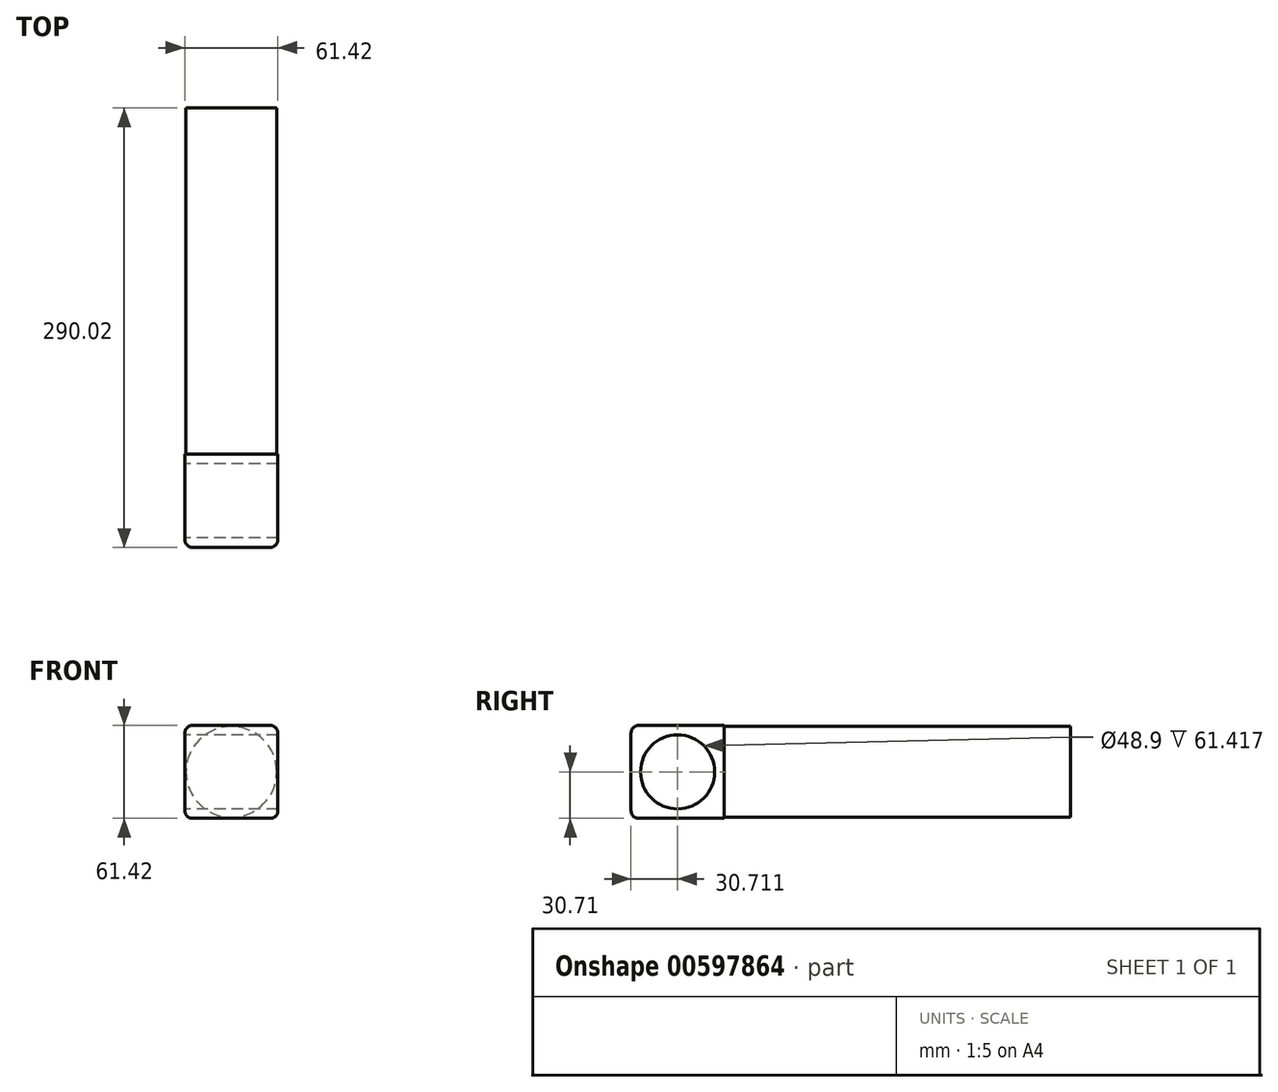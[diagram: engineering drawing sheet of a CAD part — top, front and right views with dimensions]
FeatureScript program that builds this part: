
annotation { "Feature Type Name" : "Feature", "Feature Type Description" : "" }
export const myFeature = defineFeature(function(context is Context, id is Id, definition is map)
    precondition{}
    {
        {
            var Q0;
            Q0=qCreatedBy(makeId("Front.planeOp"),FACE);
            var sketch = newSketch(context, id + "F0", { "sketchPlane" : qUnion([Q0])});
            skCircle(sketch, "E0", {"center": v(0, 0) * mm, "radius": 29.97 * mm});
            skSolve(sketch);
        }
        {
            var Q0;
            Q0=makeQuery(id+"F0.imprint","IMPRINT",FACE,{"disambiguationData":[TD([[makeQuery(id+"F0.imprint","IMPRINT",EDGE,{"derivedFrom":sQuery(id+"F0.wireOp",EDGE,"E0")}),1.0]])]});
            extrude(context, id + "F1", {"entities" : qUnion([Q0]), "oppositeDirection" : true, "depth" : 228.6 * mm, "offsetDistance" : 25.4 * mm});
        }
        {
            var Q0;
            Q0=qCreatedBy(makeId("Front.planeOp"),FACE);
            var sketch = newSketch(context, id + "F2", { "sketchPlane" : qUnion([Q0])});
            skLineSegment(sketch, "E1.bottom", {"start": v(-30.7, 30.71) * mm, "end": v(30.7, 30.71) * mm});
            skLineSegment(sketch, "E1.top", {"start": v(-30.7, -30.71) * mm, "end": v(30.7, -30.71) * mm});
            skLineSegment(sketch, "E1.left", {"start": v(-30.7, 30.71) * mm, "end": v(-30.7, -30.71) * mm});
            skLineSegment(sketch, "E1.right", {"start": v(30.7, 30.71) * mm, "end": v(30.7, -30.71) * mm});
            skPoint(sketch, "E1.middle", {"position": v(0, 0) * mm});
            skSolve(sketch);
        }
        {
            var Q0;
            Q0 = qSketchRegion(id + "F2", true);
            extrude(context, id + "F3", {"entities" : qUnion([Q0]), "operationType" : NewBodyOperationType.ADD, "depth" : 61.42 * mm, "offsetDistance" : 25.4 * mm});
        }
        {
            var Q0;
            Q0=makeQuery(id+"F3.opExtrude","SWEPT_FACE",FACE,{"disambiguationData":[OSD([sQuery(id+"F2.wireOp",EDGE,"E1.left")])]});
            var sketch = newSketch(context, id + "F4", { "sketchPlane" : qUnion([Q0])});
            skCircle(sketch, "E2", {"center": v(30.7, 0) * mm, "radius": 24.45 * mm});
            skPoint(sketch, "E2.centerSnap0", {"position": v(30.7, 30.71) * mm});
            skSolve(sketch);
        }
        {
            var Q0;
            Q0=sQuery(id+"F4.wireOp",VERTEX,"E2.center");
            var Q1;
            Q1=makeQuery(id+"F1.opExtrude","SWEPT_BODY",BODY,{"disambiguationData":[OSD([sQuery(id+"F0.wireOp",EDGE,"E0")])]});
            hole(context, id + "F5", {"style" : HoleStyle.SIMPLE, "endStyle" : HoleEndStyle.THROUGH, "holeDiameter" : 48.9 * mm, "majorDiameter" : 6.35 * mm, "isTappedThrough" : true, "tappedDepth" : 12.7 * mm, "tapClearance" : 3, "locations" : qUnion([Q0]), "scope" : qUnion([Q1])});
        }
        {
            var Q0;
            Q0=makeQuery(id+"F3.opExtrude","SWEPT_EDGE",EDGE,{"disambiguationData":[OSD([sQuery(id+"F2.wireOp",EDGE,"E1.bottom"),sQuery(id+"F2.wireOp",EDGE,"E1.left")])]});
            var Q1;
            Q1=makeQuery(id+"F3.opExtrude","CAP_EDGE",EDGE,{"disambiguationData":[OSD([sQuery(id+"F2.wireOp",EDGE,"E1.bottom")])],"isStart":false});
            var Q2;
            Q2=makeQuery(id+"F3.opExtrude","CAP_EDGE",EDGE,{"disambiguationData":[OSD([sQuery(id+"F2.wireOp",EDGE,"E1.left")])],"isStart":false});
            var Q3;
            Q3=makeQuery(id+"F3.opExtrude","SWEPT_EDGE",EDGE,{"disambiguationData":[OSD([sQuery(id+"F2.wireOp",EDGE,"E1.bottom"),sQuery(id+"F2.wireOp",EDGE,"E1.right")])]});
            var Q4;
            Q4=makeQuery(id+"F3.opExtrude","CAP_EDGE",EDGE,{"disambiguationData":[OSD([sQuery(id+"F2.wireOp",EDGE,"E1.right")])],"isStart":false});
            var Q5;
            Q5=makeQuery(id+"F3.opExtrude","SWEPT_EDGE",EDGE,{"disambiguationData":[OSD([sQuery(id+"F2.wireOp",EDGE,"E1.top"),sQuery(id+"F2.wireOp",EDGE,"E1.right")])]});
            var Q6;
            Q6=makeQuery(id+"F3.opExtrude","CAP_EDGE",EDGE,{"disambiguationData":[OSD([sQuery(id+"F2.wireOp",EDGE,"E1.top")])],"isStart":false});
            var Q7;
            Q7=makeQuery(id+"F3.opExtrude","SWEPT_EDGE",EDGE,{"disambiguationData":[OSD([sQuery(id+"F2.wireOp",EDGE,"E1.top"),sQuery(id+"F2.wireOp",EDGE,"E1.left")])]});
            fillet(context, id + "F6", {"entities" : qUnion([Q0, Q1, Q2, Q3, Q4, Q5, Q6, Q7]), "radius" : 5.08 * mm, "tangentPropagation" : true, "allowEdgeOverflow" : false});
        }
    });
